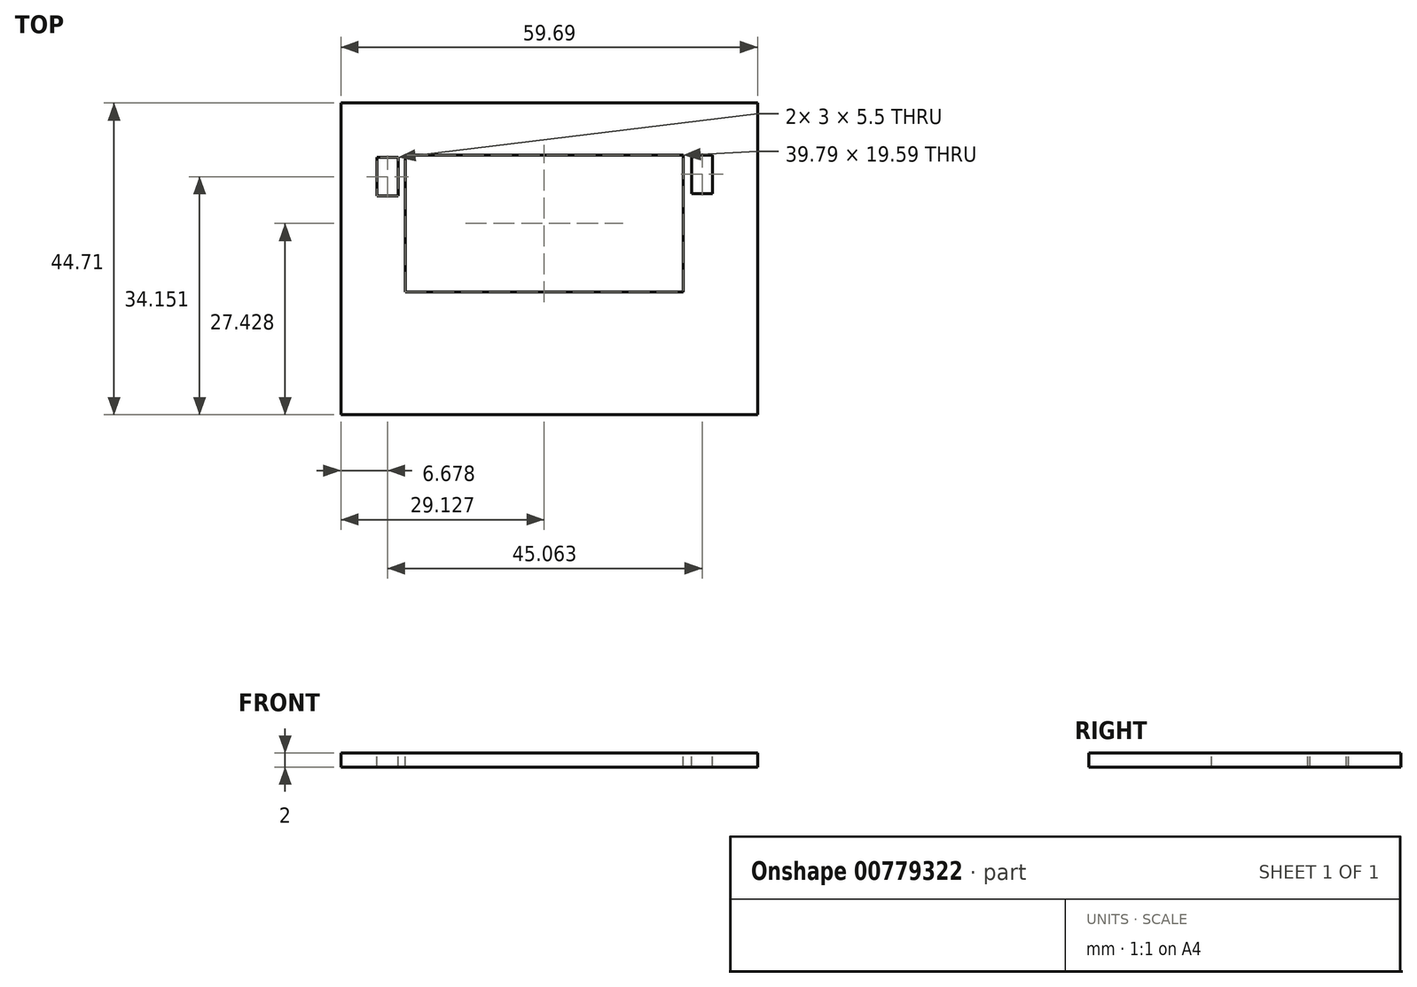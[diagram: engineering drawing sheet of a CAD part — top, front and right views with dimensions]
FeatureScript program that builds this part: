
annotation { "Feature Type Name" : "Feature", "Feature Type Description" : "" }
export const myFeature = defineFeature(function(context is Context, id is Id, definition is map)
    precondition{}
    {
        {
            var Q0;
            Q0=qCreatedBy(makeId("Top.planeOp"),FACE);
            var sketch = newSketch(context, id + "F0", { "sketchPlane" : qUnion([Q0])});
            skLineSegment(sketch, "E0.bottom", {"start": v(25, -12.83) * mm, "end": v(-25, -12.83) * mm});
            skLineSegment(sketch, "E0.top", {"start": v(25, 12.83) * mm, "end": v(-25, 12.83) * mm});
            skLineSegment(sketch, "E0.left", {"start": v(25, -12.83) * mm, "end": v(25, 12.83) * mm});
            skLineSegment(sketch, "E0.right", {"start": v(-25, -12.83) * mm, "end": v(-25, 12.83) * mm});
            skPoint(sketch, "E0.middle", {"position": v(0, 0) * mm});
            skLineSegment(sketch, "E1.bottom", {"start": v(-29.33, 17.64) * mm, "end": v(30.36, 17.64) * mm});
            skLineSegment(sketch, "E1.top", {"start": v(-29.33, -27.07) * mm, "end": v(30.36, -27.07) * mm});
            skLineSegment(sketch, "E1.left", {"start": v(-29.33, 17.64) * mm, "end": v(-29.33, -27.07) * mm});
            skLineSegment(sketch, "E1.right", {"start": v(30.36, 17.64) * mm, "end": v(30.36, -27.07) * mm});
            skLineSegment(sketch, "E2.bottom", {"start": v(-20.1, 10.15) * mm, "end": v(19.7, 10.15) * mm});
            skLineSegment(sketch, "E2.top", {"start": v(-20.1, -9.44) * mm, "end": v(19.7, -9.44) * mm});
            skLineSegment(sketch, "E2.left", {"start": v(-20.1, 10.15) * mm, "end": v(-20.1, -9.44) * mm});
            skLineSegment(sketch, "E2.right", {"start": v(19.7, 10.15) * mm, "end": v(19.7, -9.44) * mm});
            skLineSegment(sketch, "E3.bottom", {"start": v(-24.15, 9.83) * mm, "end": v(-21.15, 9.83) * mm});
            skLineSegment(sketch, "E3.top", {"start": v(-24.15, 4.33) * mm, "end": v(-21.15, 4.33) * mm});
            skLineSegment(sketch, "E3.left", {"start": v(-24.15, 9.83) * mm, "end": v(-24.15, 4.33) * mm});
            skLineSegment(sketch, "E3.right", {"start": v(-21.15, 9.83) * mm, "end": v(-21.15, 4.33) * mm});
            skLineSegment(sketch, "E4.bottom", {"start": v(23.91, 4.66) * mm, "end": v(20.91, 4.66) * mm});
            skLineSegment(sketch, "E4.top", {"start": v(23.91, 10.16) * mm, "end": v(20.91, 10.16) * mm});
            skLineSegment(sketch, "E4.left", {"start": v(23.91, 4.66) * mm, "end": v(23.91, 10.16) * mm});
            skLineSegment(sketch, "E4.right", {"start": v(20.91, 4.66) * mm, "end": v(20.91, 10.16) * mm});
            skSolve(sketch);
        }
        {
            var Q0;
            Q0=makeQuery(id+"F0.imprint","IMPRINT",FACE,{"disambiguationData":[TD([[makeQuery(id+"F0.imprint","IMPRINT",EDGE,{"derivedFrom":sQuery(id+"F0.wireOp",EDGE,"E0.bottom")}),1.0]])]});
            var Q1;
            Q1=makeQuery(id+"F0.imprint","IMPRINT",FACE,{"disambiguationData":[TD([[makeQuery(id+"F0.imprint","IMPRINT",EDGE,{"derivedFrom":sQuery(id+"F0.wireOp",EDGE,"E0.bottom")}),-1.0]])]});
            extrude(context, id + "F1", {"entities" : qUnion([Q0, Q1]), "oppositeDirection" : true, "depth" : 2 * mm, "offsetDistance" : 25 * mm});
        }
    });
